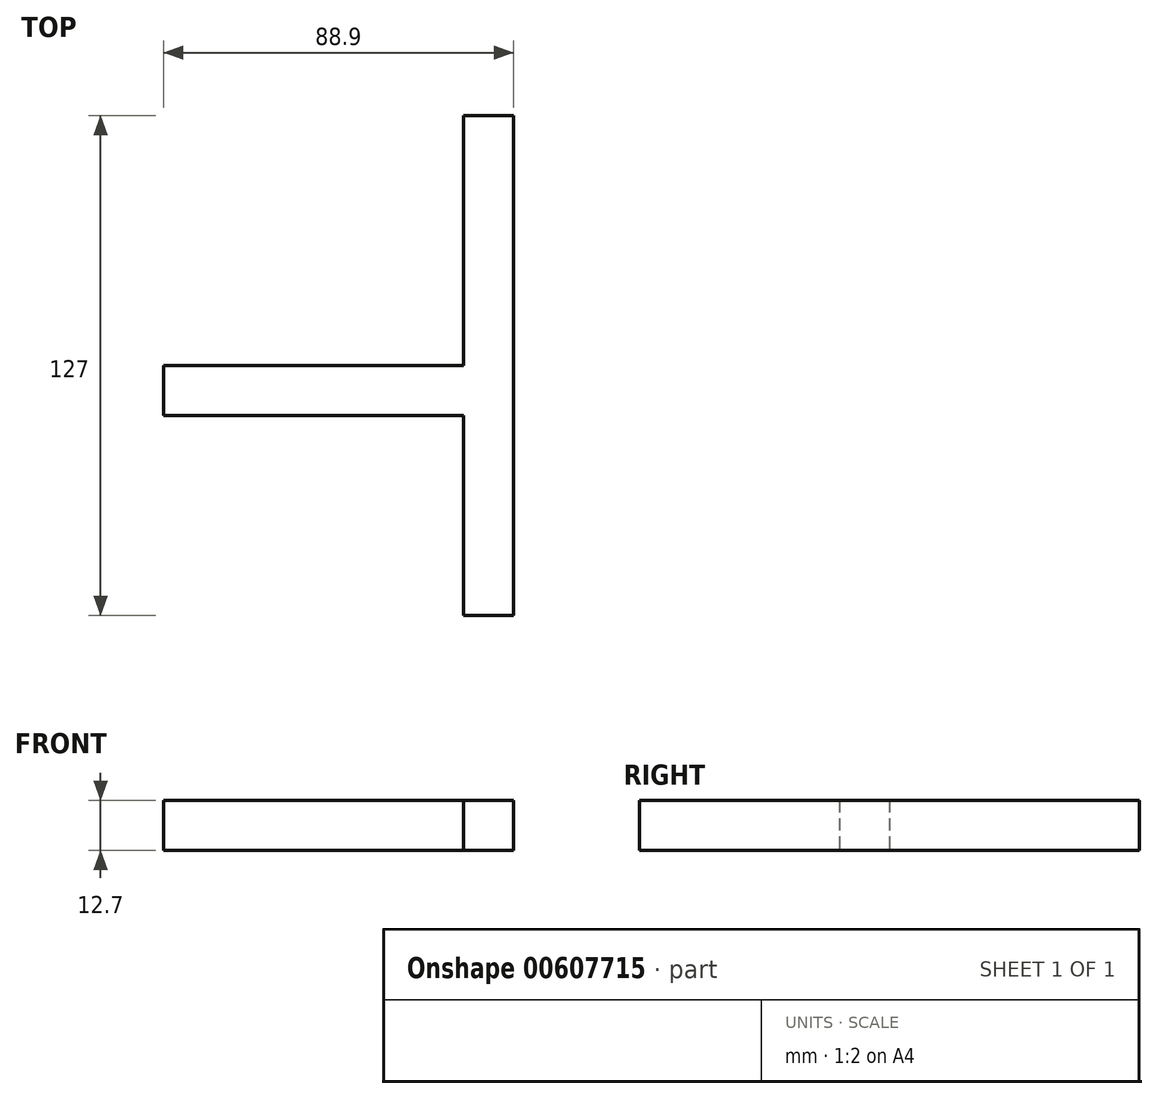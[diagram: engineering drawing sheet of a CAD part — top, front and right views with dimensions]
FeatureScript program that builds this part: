
annotation { "Feature Type Name" : "Feature", "Feature Type Description" : "" }
export const myFeature = defineFeature(function(context is Context, id is Id, definition is map)
    precondition{}
    {
        {
            var Q0;
            Q0=qCreatedBy(makeId("Right.planeOp"),FACE);
            var sketch = newSketch(context, id + "F0", { "sketchPlane" : qUnion([Q0])});
            skLineSegment(sketch, "E0.bottom", {"start": v(-63.5, 6.35) * mm, "end": v(63.5, 6.35) * mm});
            skLineSegment(sketch, "E0.top", {"start": v(-63.5, -6.35) * mm, "end": v(63.5, -6.35) * mm});
            skLineSegment(sketch, "E0.left", {"start": v(-63.5, 6.35) * mm, "end": v(-63.5, -6.35) * mm});
            skLineSegment(sketch, "E0.right", {"start": v(63.5, 6.35) * mm, "end": v(63.5, -6.35) * mm});
            skPoint(sketch, "E0.middle", {"position": v(0, 0) * mm});
            skSolve(sketch);
        }
        {
            var Q0;
            Q0 = qSketchRegion(id + "F0", true);
            extrude(context, id + "F1", {"entities" : qUnion([Q0]), "depth" : 12.7 * mm, "offsetDistance" : 25.4 * mm});
        }
        {
            var Q0;
            Q0=qCreatedBy(makeId("Front.planeOp"),FACE);
            var sketch = newSketch(context, id + "F2", { "sketchPlane" : qUnion([Q0])});
            skLineSegment(sketch, "E1.bottom", {"start": v(0, 6.35) * mm, "end": v(-76.2, 6.35) * mm});
            skLineSegment(sketch, "E1.top", {"start": v(0, -6.35) * mm, "end": v(-76.2, -6.35) * mm});
            skLineSegment(sketch, "E1.left", {"start": v(0, 6.35) * mm, "end": v(0, -6.35) * mm});
            skLineSegment(sketch, "E1.right", {"start": v(-76.2, 6.35) * mm, "end": v(-76.2, -6.35) * mm});
            skPoint(sketch, "E1.middle", {"position": v(-38.1, 0) * mm});
            skSolve(sketch);
        }
        {
            var Q0;
            Q0 = qSketchRegion(id + "F2", true);
            extrude(context, id + "F3", {"entities" : qUnion([Q0]), "operationType" : NewBodyOperationType.ADD, "depth" : 12.7 * mm, "offsetDistance" : 25.4 * mm});
        }
    });
